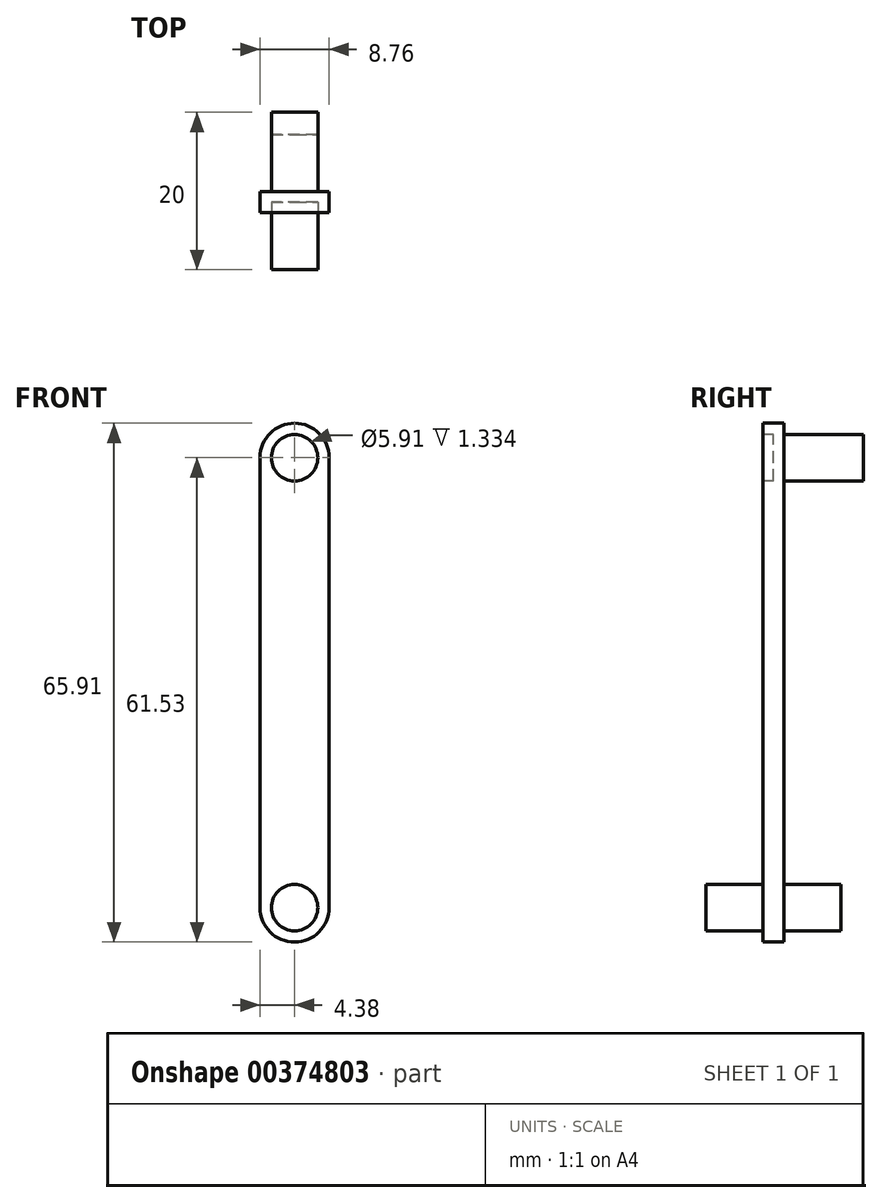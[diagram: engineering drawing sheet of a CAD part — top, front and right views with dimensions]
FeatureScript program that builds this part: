
annotation { "Feature Type Name" : "Feature", "Feature Type Description" : "" }
export const myFeature = defineFeature(function(context is Context, id is Id, definition is map)
    precondition{}
    {
        {
            var Q0;
            Q0=qCreatedBy(makeId("Front.planeOp"),FACE);
            var sketch = newSketch(context, id + "F0", { "sketchPlane" : qUnion([Q0])});
            skLineSegment(sketch, "E0", {"start": v(-0.58, 7.62) * mm, "end": v(-0.58, 0) * mm});
            skLineSegment(sketch, "E1", {"start": v(0.58, 7.62) * mm, "end": v(0.58, 0) * mm});
            skArc(sketch, "E2", {"start": v(0, 8.2) * mm, "mid": v(-0.41, 8.03) * mm, "end": v(-0.58, 7.62) * mm});
            skArc(sketch, "E3", {"start": v(0.58, 7.62) * mm, "mid": v(0.41, 8.03) * mm, "end": v(0, 8.2) * mm});
            skArc(sketch, "E4", {"start": v(-0.58, 0) * mm, "mid": v(-0.41, -0.41) * mm, "end": v(0, -0.58) * mm});
            skArc(sketch, "E5", {"start": v(0, -0.58) * mm, "mid": v(0.41, -0.41) * mm, "end": v(0.58, 0) * mm});
            skCircle(sketch, "E6", {"center": v(0, 7.62) * mm, "radius": 0.4 * mm});
            skCircle(sketch, "E7", {"center": v(0, 0) * mm, "radius": 0.4 * mm});
            skLineSegment(sketch, "E8", {"start": v(-0.4, 7.62) * mm, "end": v(-0.4, 6.73) * mm});
            skLineSegment(sketch, "E9", {"start": v(0.4, 7.62) * mm, "end": v(0.4, 6.73) * mm});
            skSolve(sketch);
        }
        {
            var Q0;
            Q0=makeQuery(id+"F0.imprint","IMPRINT",FACE,{"disambiguationData":[TD([[makeQuery(id+"F0.imprint","IMPRINT",EDGE,{"derivedFrom":sQuery(id+"F0.wireOp",EDGE,"E0")}),1.0]])]});
            extrude(context, id + "F1", {"entities" : qUnion([Q0]), "endBound" : BoundingType.SYMMETRIC, "oppositeDirection" : true, "depth" : 0.36 * mm, "offsetDistance" : 25.4 * mm});
        }
        {
            var Q0;
            Q0=makeQuery(id+"F0.imprint","IMPRINT",FACE,{"disambiguationData":[TD([[makeQuery(id+"F0.imprint","IMPRINT",EDGE,{"derivedFrom":sQuery(id+"F0.wireOp",EDGE,"E7")}),1.0]])]});
            extrude(context, id + "F2", {"entities" : qUnion([Q0]), "operationType" : NewBodyOperationType.ADD, "endBound" : BoundingType.SYMMETRIC, "depth" : 2.3 * mm, "offsetDistance" : 25.4 * mm});
        }
        {
            var Q0;
            Q0=makeQuery(id+"F0.imprint","IMPRINT",FACE,{"disambiguationData":[TD([[makeQuery(id+"F0.imprint","IMPRINT",EDGE,{"derivedFrom":sQuery(id+"F0.wireOp",EDGE,"E6")}),1.0]])]});
            extrude(context, id + "F3", {"entities" : qUnion([Q0]), "operationType" : NewBodyOperationType.ADD, "oppositeDirection" : true, "depth" : 1.52 * mm});
        }
        {
            var Q0;
            Q0=makeQuery(id+"F1.opExtrude","SWEPT_BODY",BODY,{"disambiguationData":[OSD([sQuery(id+"F0.wireOp",EDGE,"E0"),sQuery(id+"F0.wireOp",EDGE,"E1"),sQuery(id+"F0.wireOp",EDGE,"E2"),sQuery(id+"F0.wireOp",EDGE,"E3"),sQuery(id+"F0.wireOp",EDGE,"E4"),sQuery(id+"F0.wireOp",EDGE,"E5"),sQuery(id+"F0.wireOp",EDGE,"E6"),sQuery(id+"F0.wireOp",EDGE,"E7")])]});
            var Q1;
            Q1=qCreatedBy(makeId("Origin.pointOp"),VERTEX);
            transform(context, id + "F4", {"entities" : qUnion([Q0]), "transformType" : TransformType.SCALE_UNIFORMLY, "scale" : 7.5, "scalePoint" : qUnion([Q1]), "makeCopy" : false});
        }
    });
